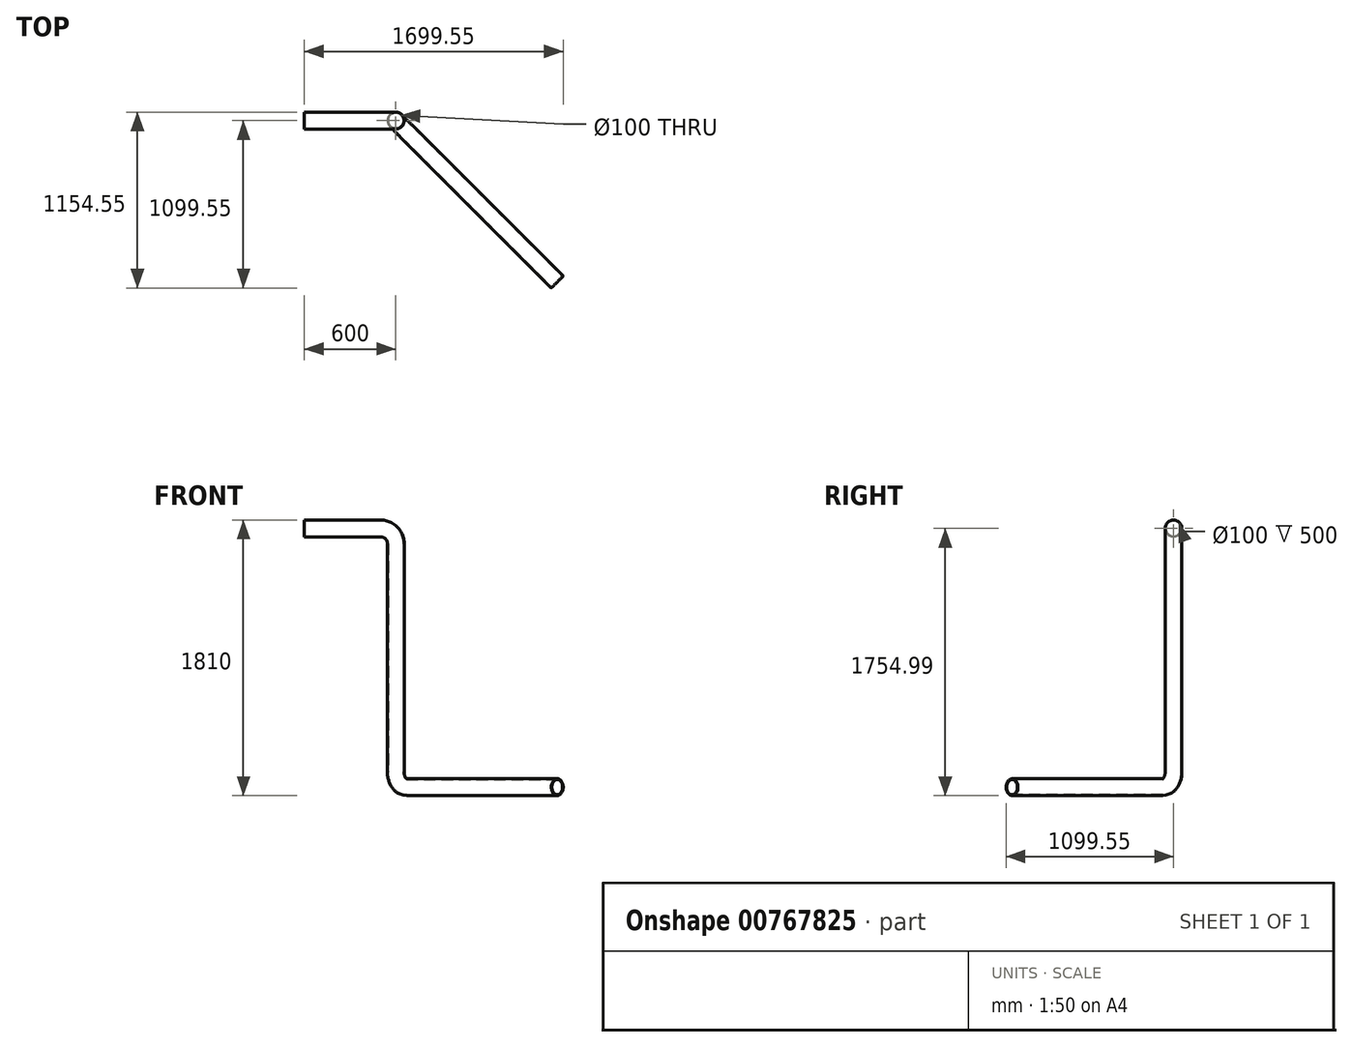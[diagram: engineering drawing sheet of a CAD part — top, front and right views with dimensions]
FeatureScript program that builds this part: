
annotation { "Feature Type Name" : "Feature", "Feature Type Description" : "" }
export const myFeature = defineFeature(function(context is Context, id is Id, definition is map)
    precondition{}
    {
        {
            var Q0;
            Q0=qCreatedBy(makeId("Front.planeOp"),FACE);
            var sketch = newSketch(context, id + "F0", { "sketchPlane" : qUnion([Q0])});
            skLineSegment(sketch, "E0", {"start": v(-100, 143.32) * mm, "end": v(-600, 143.32) * mm});
            skLineSegment(sketch, "E1", {"start": v(0, 43.32) * mm, "end": v(0, -1556.68) * mm});
            skPoint(sketch, "E2.visualSharp", {"position": v(0, 143.32) * mm});
            skArc(sketch, "E2.filletArc", {"start": v(0, 43.32) * mm, "mid": v(-29.29, 114.03) * mm, "end": v(-100, 143.32) * mm});
            skSolve(sketch);
        }
        {
            var Q0;
            Q0=qCreatedBy(makeId("Right.planeOp"),FACE);
            var Q1;
            Q1=sQuery(id+"F0.wireOp",VERTEX,"E0.end");
            cPlane(context, id + "F1", {"entities" : qUnion([Q0, Q1]), "cplaneType" : CPlaneType.PLANE_POINT, "offset" : 25 * mm, "width" : 150 * mm, "height" : 150 * mm});
        }
        {
            var Q0;
            Q0=qCreatedBy(id+"F1.planeOp",FACE);
            var sketch = newSketch(context, id + "F2", { "sketchPlane" : qUnion([Q0])});
            skPoint(sketch, "E3.0", {"position": v(0, 143.32) * mm});
            skCircle(sketch, "E4", {"center": v(0, 143.32) * mm, "radius": 55 * mm});
            skCircle(sketch, "E5", {"center": v(0, 143.32) * mm, "radius": 50 * mm});
            skSolve(sketch);
        }
        {
            var Q0;
            Q0=qCreatedBy(makeId("Front.planeOp"),FACE);
            var Q1;
            Q1=sQuery(id+"F0.wireOp",EDGE,"E1");
            cPlane(context, id + "F3", {"entities" : qUnion([Q0, Q1]), "cplaneType" : CPlaneType.LINE_ANGLE, "offset" : 25 * mm, "angle" : 45 * degree, "width" : 150 * mm, "height" : 150 * mm});
        }
        {
            var Q0;
            Q0=qCreatedBy(id+"F3.planeOp",FACE);
            var sketch = newSketch(context, id + "F4", { "sketchPlane" : qUnion([Q0])});
            skLineSegment(sketch, "E6.0", {"start": v(0, 43.32) * mm, "end": v(0, -1456.68) * mm});
            skLineSegment(sketch, "E7", {"start": v(-100, -1556.68) * mm, "end": v(-1500, -1556.68) * mm});
            skPoint(sketch, "E8.visualSharp", {"position": v(0, -1556.68) * mm});
            skArc(sketch, "E8.filletArc", {"start": v(-100, -1556.68) * mm, "mid": v(-29.29, -1527.4) * mm, "end": v(0, -1456.68) * mm});
            skSolve(sketch);
        }
        {
            var Q0;
            Q0=makeQuery(id+"F2.imprint","IMPRINT",FACE,{"disambiguationData":[TD([[makeQuery(id+"F2.imprint","IMPRINT",EDGE,{"derivedFrom":sQuery(id+"F2.wireOp",EDGE,"E4")}),1.0]])]});
            var Q1;
            Q1=sQuery(id+"F0.wireOp",EDGE,"E0");
            var Q2;
            Q2=sQuery(id+"F0.wireOp",EDGE,"E2.filletArc");
            var Q3;
            Q3=sQuery(id+"F4.wireOp",EDGE,"E6.0");
            var Q4;
            Q4=sQuery(id+"F4.wireOp",EDGE,"E8.filletArc");
            var Q5;
            Q5=sQuery(id+"F4.wireOp",EDGE,"E7");
            sweep(context, id + "F5", {"profiles" : qUnion([Q0]), "path" : qUnion([Q1, Q2, Q3, Q4, Q5])});
        }
    });
